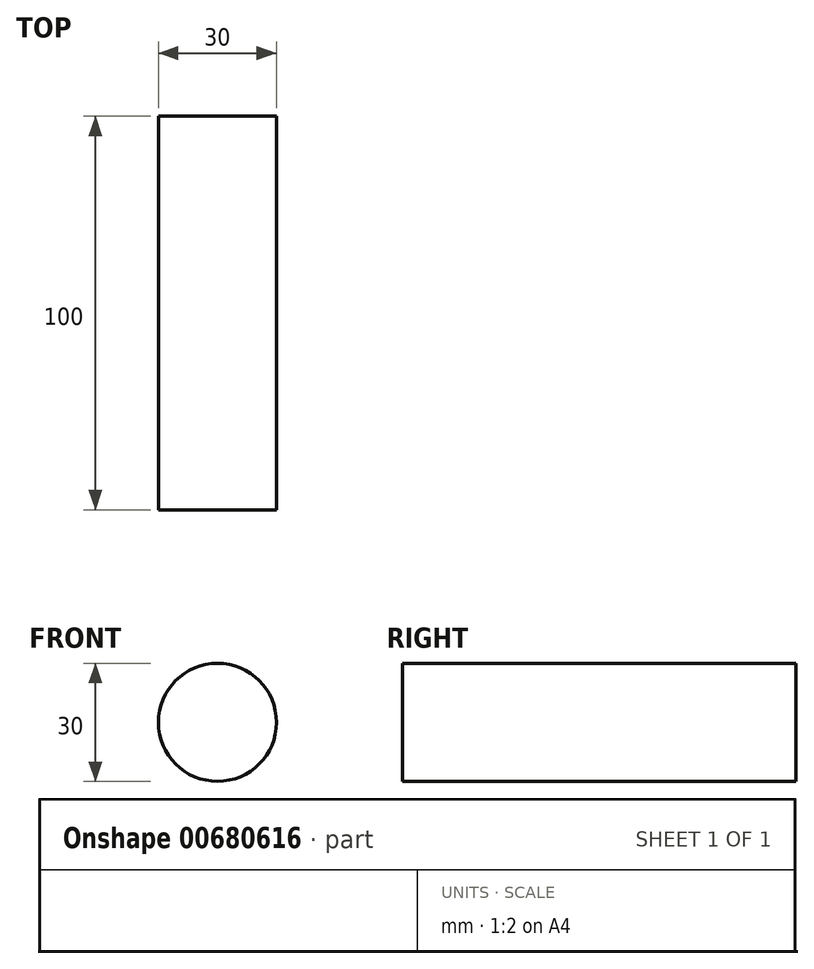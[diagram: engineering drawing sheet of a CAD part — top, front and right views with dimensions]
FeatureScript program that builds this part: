
annotation { "Feature Type Name" : "Feature", "Feature Type Description" : "" }
export const myFeature = defineFeature(function(context is Context, id is Id, definition is map)
    precondition{}
    {
        {
            var Q0;
            Q0=qCreatedBy(makeId("Front.planeOp"),FACE);
            var sketch = newSketch(context, id + "F0", { "sketchPlane" : qUnion([Q0])});
            skCircle(sketch, "E0", {"center": v(0, 0) * mm, "radius": 15 * mm});
            skSolve(sketch);
        }
        {
            var Q0;
            Q0=makeQuery(id+"F0.imprint","IMPRINT",FACE,{"disambiguationData":[TD([[makeQuery(id+"F0.imprint","IMPRINT",EDGE,{"derivedFrom":sQuery(id+"F0.wireOp",EDGE,"E0")}),1.0]])]});
            extrude(context, id + "F1", {"entities" : qUnion([Q0]), "endBound" : BoundingType.SYMMETRIC, "depth" : 100 * mm, "offsetDistance" : 25 * mm});
        }
    });
